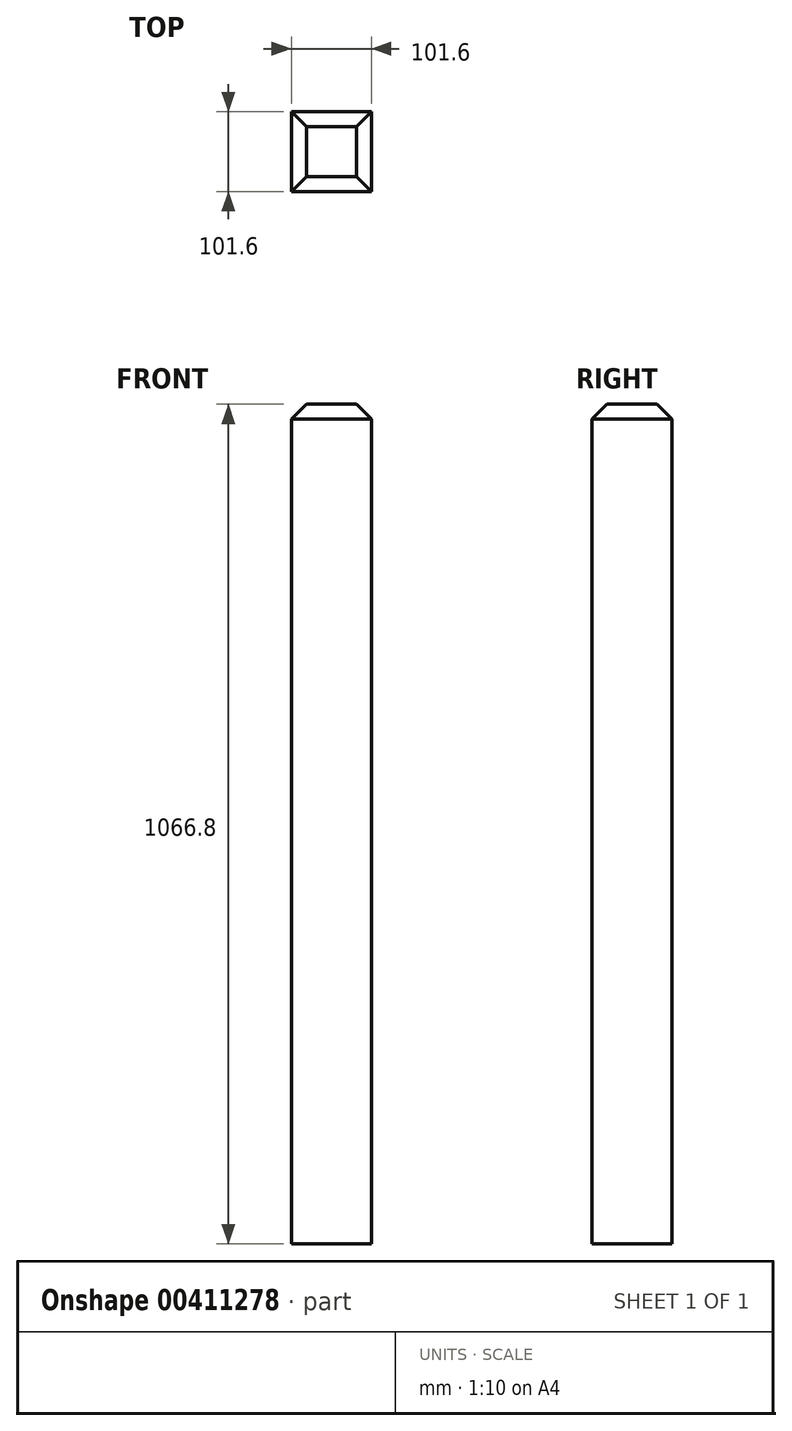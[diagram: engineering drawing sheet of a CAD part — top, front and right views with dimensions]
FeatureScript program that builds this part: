
annotation { "Feature Type Name" : "Feature", "Feature Type Description" : "" }
export const myFeature = defineFeature(function(context is Context, id is Id, definition is map)
    precondition{}
    {
        {
            var Q0;
            Q0=qCreatedBy(makeId("Top.planeOp"),FACE);
            var sketch = newSketch(context, id + "F0", { "sketchPlane" : qUnion([Q0])});
            skLineSegment(sketch, "E0.bottom", {"start": v(50.8, -50.8) * mm, "end": v(-50.8, -50.8) * mm});
            skLineSegment(sketch, "E0.top", {"start": v(50.8, 50.8) * mm, "end": v(-50.8, 50.8) * mm});
            skLineSegment(sketch, "E0.left", {"start": v(50.8, -50.8) * mm, "end": v(50.8, 50.8) * mm});
            skLineSegment(sketch, "E0.right", {"start": v(-50.8, -50.8) * mm, "end": v(-50.8, 50.8) * mm});
            skPoint(sketch, "E0.middle", {"position": v(0, 0) * mm});
            skSolve(sketch);
        }
        {
            var Q0;
            Q0=makeQuery(id+"F0.imprint","IMPRINT",FACE,{"disambiguationData":[TD([[makeQuery(id+"F0.imprint","IMPRINT",EDGE,{"derivedFrom":sQuery(id+"F0.wireOp",EDGE,"E0.bottom")}),-1.0]])]});
            extrude(context, id + "F1", {"entities" : qUnion([Q0]), "depth" : 1066.8 * mm});
        }
        {
            var Q0;
            Q0=makeQuery(id+"F1.opExtrude","CAP_EDGE",EDGE,{"disambiguationData":[OSD([sQuery(id+"F0.wireOp",EDGE,"E0.bottom")])],"isStart":false});
            var Q1;
            Q1=makeQuery(id+"F1.opExtrude","CAP_EDGE",EDGE,{"disambiguationData":[OSD([sQuery(id+"F0.wireOp",EDGE,"E0.right")])],"isStart":false});
            var Q2;
            Q2=makeQuery(id+"F1.opExtrude","CAP_EDGE",EDGE,{"disambiguationData":[OSD([sQuery(id+"F0.wireOp",EDGE,"E0.left")])],"isStart":false});
            var Q3;
            Q3=makeQuery(id+"F1.opExtrude","CAP_EDGE",EDGE,{"disambiguationData":[OSD([sQuery(id+"F0.wireOp",EDGE,"E0.top")])],"isStart":false});
            chamfer(context, id + "F2", {"entities" : qUnion([Q0, Q1, Q2, Q3]), "width" : 19.05 * mm, "tangentPropagation" : true});
        }
    });
